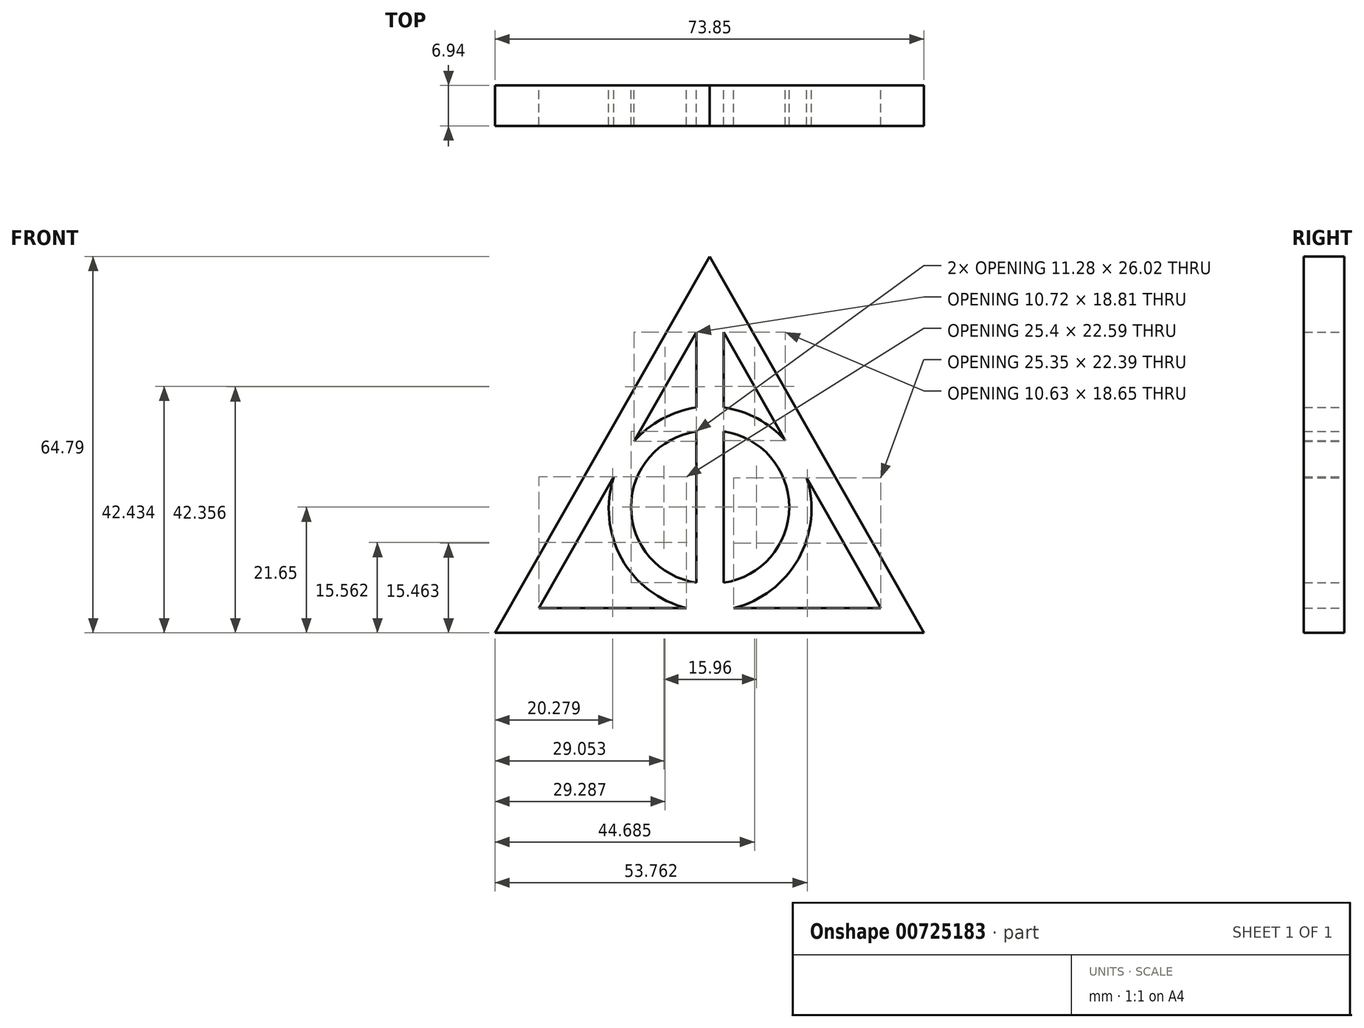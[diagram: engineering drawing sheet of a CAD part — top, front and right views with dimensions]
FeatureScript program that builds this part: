
annotation { "Feature Type Name" : "Feature", "Feature Type Description" : "" }
export const myFeature = defineFeature(function(context is Context, id is Id, definition is map)
    precondition{}
    {
        {
            var Q0;
            Q0=qCreatedBy(makeId("Front.planeOp"),FACE);
            var sketch = newSketch(context, id + "F0", { "sketchPlane" : qUnion([Q0])});
            skPoint(sketch, "E0", {"position": v(-4.67, -23.75) * mm});
            skPoint(sketch, "E1", {"position": v(0, -23.75) * mm});
            skPoint(sketch, "E2", {"position": v(0, -49.77) * mm});
            skPoint(sketch, "E3", {"position": v(-4.67, -49.77) * mm});
            skArc(sketch, "E4", {"start": v(0, -49.77) * mm, "mid": v(11.28, -36.76) * mm, "end": v(0, -23.75) * mm});
            skArc(sketch, "E5", {"start": v(-4.67, -23.75) * mm, "mid": v(-15.96, -36.76) * mm, "end": v(-4.67, -49.77) * mm});
            skArc(sketch, "E6", {"start": v(1.43, -54.2) * mm, "mid": v(15.1, -36.32) * mm, "end": v(0, -19.62) * mm});
            skArc(sketch, "E7", {"start": v(-4.67, -19.62) * mm, "mid": v(-19.78, -36.32) * mm, "end": v(-6.1, -54.2) * mm});
            skLineSegment(sketch, "E8", {"start": v(-4.67, -23.75) * mm, "end": v(-4.67, -49.77) * mm});
            skLineSegment(sketch, "E9", {"start": v(0, -23.75) * mm, "end": v(0, -49.77) * mm});
            skArc(sketch, "E10", {"start": v(-6.1, -54.2) * mm, "mid": v(-2.34, -54.56) * mm, "end": v(1.43, -54.2) * mm});
            skArc(sketch, "E11", {"start": v(0, -19.62) * mm, "mid": v(-2.34, -19.36) * mm, "end": v(-4.67, -19.62) * mm});
            skSolve(sketch);
        }
        {
            var Q0;
            Q0=makeQuery(id+"F0.imprint","IMPRINT",FACE,{"disambiguationData":[TD([[makeQuery(id+"F0.imprint","IMPRINT",EDGE,{"derivedFrom":sQuery(id+"F0.wireOp",EDGE,"E4")}),-1.0]])]});
            extrude(context, id + "F1", {"entities" : qUnion([Q0]), "endBound" : BoundingType.SYMMETRIC, "depth" : 6.93 * mm, "offsetDistance" : 25.4 * mm});
        }
        {
            var Q0;
            Q0=qCreatedBy(makeId("Front.planeOp"),FACE);
            var sketch = newSketch(context, id + "F2", { "sketchPlane" : qUnion([Q0])});
            skLineSegment(sketch, "E12", {"start": v(0, -6.65) * mm, "end": v(27.07, -54.14) * mm});
            skLineSegment(sketch, "E13", {"start": v(27.07, -54.14) * mm, "end": v(-31.79, -54.14) * mm});
            skLineSegment(sketch, "E14", {"start": v(-31.79, -54.14) * mm, "end": v(-4.72, -6.65) * mm});
            skLineSegment(sketch, "E15", {"start": v(-2.44, 6.38) * mm, "end": v(-39.37, -58.41) * mm});
            skLineSegment(sketch, "E16", {"start": v(-39.37, -58.41) * mm, "end": v(34.48, -58.41) * mm});
            skLineSegment(sketch, "E17", {"start": v(34.48, -58.41) * mm, "end": v(-2.44, 6.38) * mm});
            skLineSegment(sketch, "E18", {"start": v(-4.72, -6.65) * mm, "end": v(-4.72, -19.75) * mm});
            skLineSegment(sketch, "E19", {"start": v(0, -6.65) * mm, "end": v(0, -19.75) * mm});
            skArc(sketch, "E20", {"start": v(0, -19.75) * mm, "mid": v(-2.36, -19.4) * mm, "end": v(-4.72, -19.75) * mm});
            skSolve(sketch);
        }
        {
            var Q0;
            Q0=makeQuery(id+"F2.imprint","IMPRINT",FACE,{"disambiguationData":[TD([[makeQuery(id+"F2.imprint","IMPRINT",EDGE,{"derivedFrom":sQuery(id+"F2.wireOp",EDGE,"E12")}),1.0]])]});
            extrude(context, id + "F3", {"entities" : qUnion([Q0]), "operationType" : NewBodyOperationType.ADD, "endBound" : BoundingType.SYMMETRIC, "depth" : 6.93 * mm, "offsetDistance" : 25.4 * mm});
        }
    });
